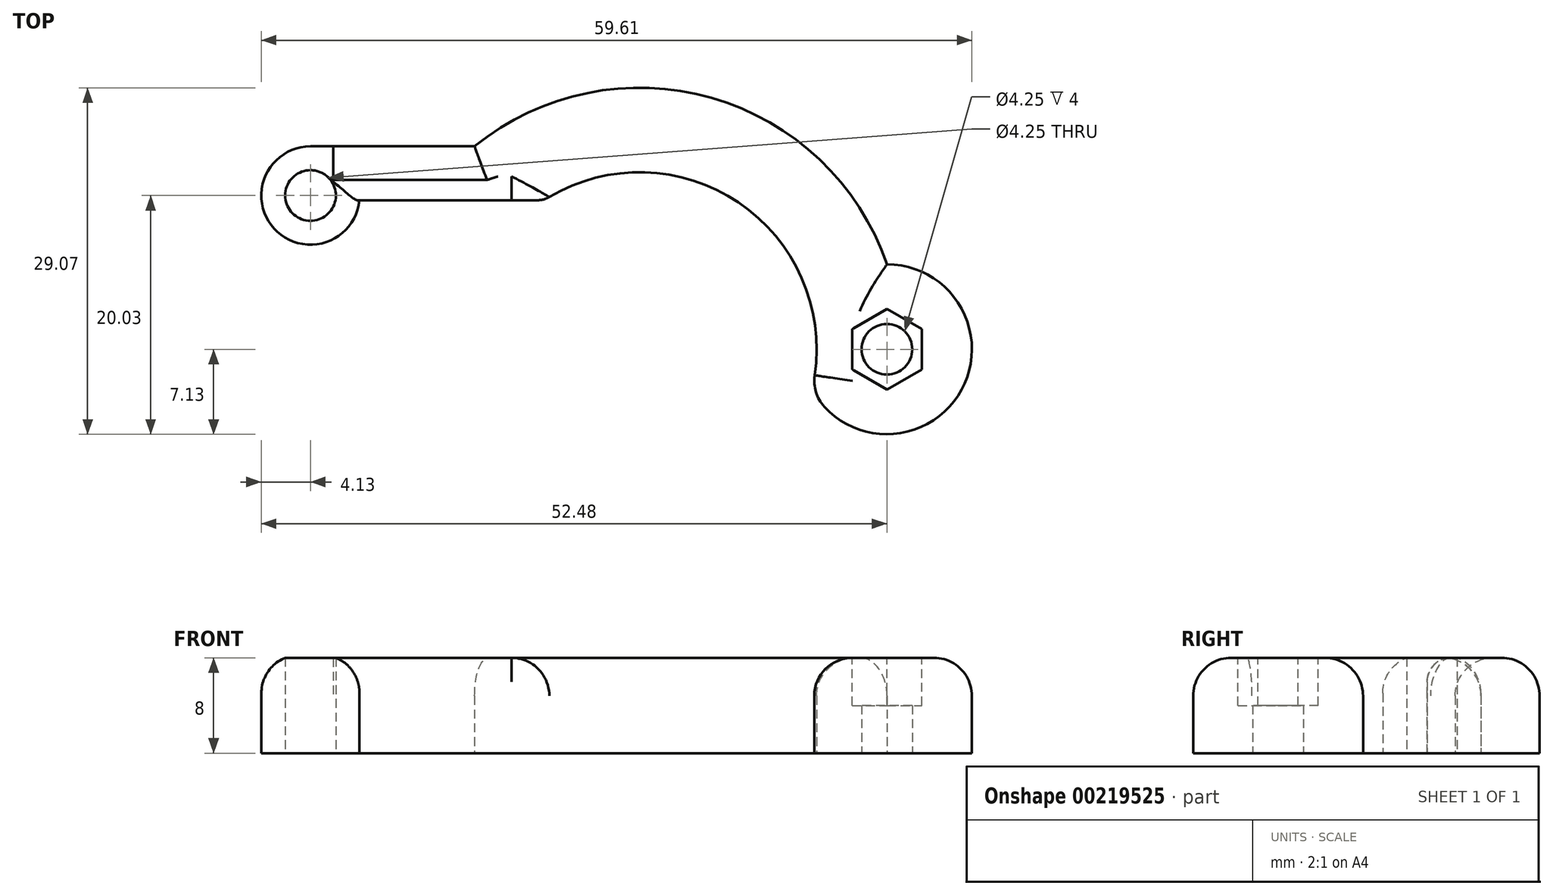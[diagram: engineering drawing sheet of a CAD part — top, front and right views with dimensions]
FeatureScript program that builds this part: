
annotation { "Feature Type Name" : "Feature", "Feature Type Description" : "" }
export const myFeature = defineFeature(function(context is Context, id is Id, definition is map)
    precondition{}
    {
        {
            var Q0;
            Q0=qCreatedBy(makeId("Top.planeOp"),FACE);
            var sketch = newSketch(context, id + "F0", { "sketchPlane" : qUnion([Q0])});
            skArc(sketch, "E0", {"start": v(-21.54, 9.93) * mm, "mid": v(-17.16, -12.23) * mm, "end": v(-1.44, 4) * mm, "construction": true});
            skCircle(sketch, "E1", {"center": v(14.05, 0) * mm, "radius": 13.25 * mm, "construction": true});
            skCircle(sketch, "E2", {"center": v(-13.55, 0) * mm, "radius": 6.5 * mm, "construction": true});
            skArc(sketch, "E3", {"start": v(27.3, 0) * mm, "mid": v(14.05, -13.25) * mm, "end": v(0.8, 0) * mm, "construction": true});
            skArc(sketch, "E4", {"start": v(-26.45, 0) * mm, "mid": v(-25.17, 5.6) * mm, "end": v(-21.6, 10.08) * mm, "construction": true});
            skLineSegment(sketch, "E5", {"start": v(-0.65, 0) * mm, "end": v(0.8, 0) * mm, "construction": true});
            skLineSegment(sketch, "E6", {"start": v(27.3, 0) * mm, "end": v(34.8, 0) * mm, "construction": true});
            skLineSegment(sketch, "E7", {"start": v(-26.45, -132) * mm, "end": v(-51.45, -132) * mm, "construction": true});
            skLineSegment(sketch, "E8", {"start": v(-51.45, -132) * mm, "end": v(-51.45, -140) * mm, "construction": true});
            skLineSegment(sketch, "E9", {"start": v(-51.45, -140) * mm, "end": v(51.45, -140) * mm, "construction": true});
            skLineSegment(sketch, "E10", {"start": v(51.45, -140) * mm, "end": v(51.45, -132) * mm, "construction": true});
            skLineSegment(sketch, "E11", {"start": v(51.45, -132) * mm, "end": v(26.45, -132) * mm, "construction": true});
            skLineSegment(sketch, "E12", {"start": v(26.45, -132) * mm, "end": v(26.45, -16.64) * mm, "construction": true});
            skPoint(sketch, "E13.visualSharp", {"position": v(-12.5, -132) * mm});
            skLineSegment(sketch, "E13.filletArc", {"start": v(-26.45, -132) * mm, "end": v(-26.45, -132) * mm});
            skPoint(sketch, "E14.visualSharp", {"position": v(26.45, -132) * mm});
            skLineSegment(sketch, "E14.filletArc", {"start": v(26.45, -132) * mm, "end": v(26.45, -132) * mm});
            skArc(sketch, "E15", {"start": v(34.8, 0) * mm, "mid": v(32.6, -9.3) * mm, "end": v(26.45, -16.64) * mm, "construction": true});
            skCircle(sketch, "E16", {"center": v(0, -28.75) * mm, "radius": 16 * mm, "construction": true});
            skCircle(sketch, "E17", {"center": v(0, -28.75) * mm, "radius": 2.12 * mm, "construction": true});
            skCircle(sketch, "E18", {"center": v(14.05, 0) * mm, "radius": 16 * mm, "construction": true});
            skLineSegment(sketch, "E19.MirrorCS", {"start": v(-26.45, -132) * mm, "end": v(-26.45, -71.5) * mm, "construction": true});
            skCircle(sketch, "E20", {"center": v(-40, -57) * mm, "radius": 6.5 * mm, "construction": true});
            skArc(sketch, "E21", {"start": v(-40, -42.5) * mm, "mid": v(-40.1, -42.5) * mm, "end": v(-40.18, -42.5) * mm, "construction": true});
            skLineSegment(sketch, "E22", {"start": v(-26.45, -71.5) * mm, "end": v(-40, -71.5) * mm, "construction": true});
            skCircle(sketch, "E23", {"center": v(14.05, -57) * mm, "radius": 6.5 * mm, "construction": true});
            skCircle(sketch, "E24", {"center": v(-32, -28.75) * mm, "radius": 2.12 * mm, "construction": true});
            skCircle(sketch, "E25", {"center": v(-32, -28.75) * mm, "radius": 16 * mm, "construction": true});
            skLineSegment(sketch, "E26", {"start": v(-54.5, -57) * mm, "end": v(-54.5, 0) * mm, "construction": true});
            skLineSegment(sketch, "E27", {"start": v(-54.5, 0) * mm, "end": v(-26.45, 0) * mm, "construction": true});
            skArc(sketch, "E28.trimOffspring", {"start": v(-54.5, -57) * mm, "mid": v(-50.25, -67.25) * mm, "end": v(-40, -71.5) * mm, "construction": true});
            skArc(sketch, "E29", {"start": v(-5.5, 10.08) * mm, "mid": v(-13.63, 21.42) * mm, "end": v(-21.54, 9.93) * mm, "construction": true});
            skCircle(sketch, "E30", {"center": v(-13.55, 12.9) * mm, "radius": 2.12 * mm});
            skArc(sketch, "E31.trimOffspring", {"start": v(-11.45, 12.58) * mm, "mid": v(-13.55, 12.75) * mm, "end": v(-15.65, 12.58) * mm, "construction": true});
            skArc(sketch, "E32.trimOffspring", {"start": v(-5.5, 10.08) * mm, "mid": v(-1.93, 5.6) * mm, "end": v(-0.65, 0) * mm, "construction": true});
            skArc(sketch, "E33", {"start": v(34.8, 8.52) * mm, "mid": v(43.28, -0.88) * mm, "end": v(33.05, -8.34) * mm, "construction": true});
            skCircle(sketch, "E34", {"center": v(34.8, 0) * mm, "radius": 2.12 * mm});
            skLineSegment(sketch, "E35", {"start": v(27.3, 0) * mm, "end": v(34.8, 8.52) * mm, "construction": true});
            skArc(sketch, "E36", {"start": v(-13.55, 17.03) * mm, "mid": v(-16.6, 10.13) * mm, "end": v(-9.44, 12.5) * mm});
            skArc(sketch, "E37", {"start": v(28.52, -3.36) * mm, "mid": v(40.91, -3.66) * mm, "end": v(34.8, 7.12) * mm});
            skArc(sketch, "E38", {"start": v(34.8, 7.12) * mm, "mid": v(20.09, 21.1) * mm, "end": v(0.21, 17.03) * mm});
            skArc(sketch, "E39", {"start": v(28.8, 1.7) * mm, "mid": v(20.41, 13.42) * mm, "end": v(6.03, 12.5) * mm});
            skArc(sketch, "E40", {"start": v(28.8, 1.7) * mm, "mid": v(28.88, -0.84) * mm, "end": v(28.52, -3.36) * mm});
            skLineSegment(sketch, "E41", {"start": v(-13.55, 17.03) * mm, "end": v(0.21, 17.03) * mm});
            skLineSegment(sketch, "E42", {"start": v(-9.44, 12.5) * mm, "end": v(6.03, 12.5) * mm});
            skSolve(sketch);
        }
        {
            var Q0;
            Q0=qSketchRegion(id+"F0",true);
            extrude(context, id + "F1", {"entities" : qUnion([Q0]), "depth" : 8 * mm});
        }
        {
            var Q0;
            Q0=makeQuery(id+"F1.opExtrude","CAP_FACE",FACE,{"disambiguationData":[OSD([sQuery(id+"F0.wireOp",EDGE,"E30"),sQuery(id+"F0.wireOp",EDGE,"E34"),sQuery(id+"F0.wireOp",EDGE,"E36"),sQuery(id+"F0.wireOp",EDGE,"E37"),sQuery(id+"F0.wireOp",EDGE,"E38"),sQuery(id+"F0.wireOp",EDGE,"E39"),sQuery(id+"F0.wireOp",EDGE,"E40"),sQuery(id+"F0.wireOp",EDGE,"E41"),sQuery(id+"F0.wireOp",EDGE,"E42")])],"isStart":false});
            var sketch = newSketch(context, id + "F2", { "sketchPlane" : qUnion([Q0])});
            skCircle(sketch, "E43.cCircle", {"center": v(34.8, 0) * mm, "radius": 2.92 * mm, "construction": true});
            skLineSegment(sketch, "E43.0", {"start": v(37.72, 1.68) * mm, "end": v(37.72, -1.68) * mm});
            skLineSegment(sketch, "E43.1", {"start": v(37.72, -1.68) * mm, "end": v(34.8, -3.37) * mm});
            skLineSegment(sketch, "E43.2", {"start": v(34.8, -3.37) * mm, "end": v(31.88, -1.68) * mm});
            skLineSegment(sketch, "E43.3", {"start": v(31.88, -1.68) * mm, "end": v(31.88, 1.68) * mm});
            skLineSegment(sketch, "E43.4", {"start": v(31.88, 1.68) * mm, "end": v(34.8, 3.37) * mm});
            skLineSegment(sketch, "E43.5", {"start": v(34.8, 3.37) * mm, "end": v(37.72, 1.68) * mm});
            skPoint(sketch, "E43.0.midPoint", {"position": v(37.72, 0) * mm});
            skSolve(sketch);
        }
        {
            var Q0;
            Q0 = qSketchRegion(id + "F2", true);
            extrude(context, id + "F3", {"entities" : qUnion([Q0]), "operationType" : NewBodyOperationType.REMOVE, "oppositeDirection" : true, "depth" : 4 * mm});
        }
        {
            var Q0;
            Q0=makeQuery(id+"F1.opExtrude","CAP_EDGE",EDGE,{"disambiguationData":[OSD([sQuery(id+"F0.wireOp",EDGE,"E38")])],"isStart":false});
            var Q1;
            Q1=makeQuery(id+"F1.opExtrude","CAP_EDGE",EDGE,{"disambiguationData":[OSD([sQuery(id+"F0.wireOp",EDGE,"E41")])],"isStart":false});
            var Q2;
            Q2=makeQuery(id+"F1.opExtrude","CAP_EDGE",EDGE,{"disambiguationData":[OSD([sQuery(id+"F0.wireOp",EDGE,"E39"),sQuery(id+"F0.wireOp",EDGE,"E40")])],"isStart":false});
            fillet(context, id + "F4", {"entities" : qUnion([Q0, Q1, Q2]), "radius" : 3.2 * mm, "tangentPropagation" : true, "allowEdgeOverflow" : false});
        }
        {
            var Q0;
            Q0=makeQuery(id+"F1.opExtrude","CAP_EDGE",EDGE,{"disambiguationData":[OSD([sQuery(id+"F0.wireOp",EDGE,"E37")])],"isStart":false});
            fillet(context, id + "F5", {"entities" : qUnion([Q0]), "radius" : 3.2 * mm, "tangentPropagation" : true, "allowEdgeOverflow" : false});
        }
        {
            var Q0;
            Q0=makeQuery(id+"F1.opExtrude","CAP_EDGE",EDGE,{"disambiguationData":[OSD([sQuery(id+"F0.wireOp",EDGE,"E42")])],"isStart":false});
            fillet(context, id + "F6", {"entities" : qUnion([Q0]), "radius" : 2 * mm, "tangentPropagation" : true, "allowEdgeOverflow" : false});
        }
    });
